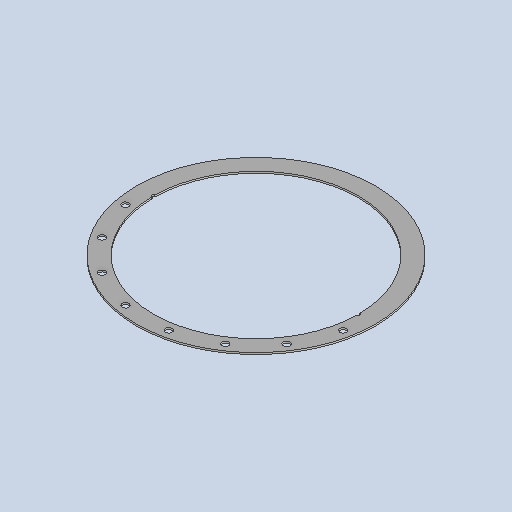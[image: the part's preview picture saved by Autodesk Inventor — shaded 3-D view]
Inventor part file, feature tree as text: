
AUTODESK INVENTOR PART (.ipt)
format: ipt  version: 2025 (Build 290162010, 162A)  size: 168,448 bytes
history: native  units: mm
features: sketch x3, extrude x2, other x2, sheet_metal_op x1, pattern_circular x1, projected_geometry x1
ambient origin geometry x8: Origin, YZ Plane, XZ Plane, XY Plane, X Axis, Y Axis, Z Axis, Center Point
bodies: Solid1 (feature_tree)
feature tree (10):
  sheet_metal_op  "Face1"
  extrude  "Extrusion1"  TaperAngle=0.0deg  [1 undecoded]
  pattern_circular  "Circular Pattern1"  Count=8 Angle=157.5deg
  extrude  "Extrusion2"  Depth=30.0mm
  sketch  "Sketch1"  dims[d2=3.0mm d4=0.0mm d5=0.0mm d6=80.0mm d7=157.5deg]
  other  "Plate1"
  sketch  "Sketch2"  dims[d9=390.0mm d11=30.0mm]
  projected_geometry  "Projected Loop1"
  sketch  "Sketch3"  dims[d20=1.963495mm d21=12.0mm d25=0.0mm d26=0.0mm d27=5.0mm d29=80.0mm d30=0.5mm d31=0.872665mm d32=0.5mm d33=0.872665mm]
  other  "Definition1"
note: 1 required parameter value undecoded (feature->parameter linkage not recoverable at this tier; creation-order binding heuristic only, values carry confidence <= 0.55)
